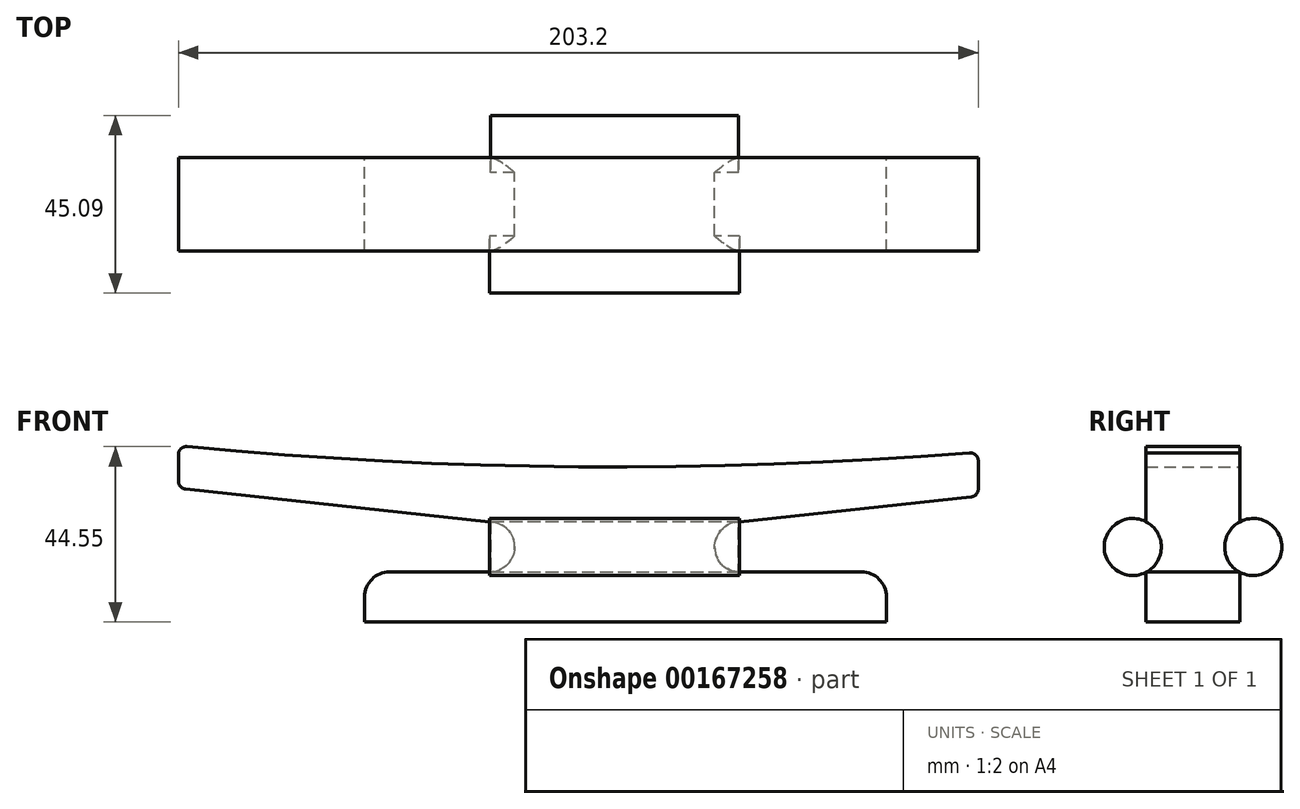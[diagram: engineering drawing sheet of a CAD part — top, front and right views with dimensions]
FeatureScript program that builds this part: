
annotation { "Feature Type Name" : "Feature", "Feature Type Description" : "" }
export const myFeature = defineFeature(function(context is Context, id is Id, definition is map)
    precondition{}
    {
        {
            var Q0;
            Q0=qCreatedBy(makeId("Front.planeOp"),FACE);
            var sketch = newSketch(context, id + "F0", { "sketchPlane" : qUnion([Q0])});
            skLineSegment(sketch, "E0", {"start": v(0, 28.03) * mm, "end": v(0, 38.16) * mm, "construction": true});
            skLineSegment(sketch, "E1", {"start": v(-63.5, -11.34) * mm, "end": v(-63.5, -4.99) * mm});
            skLineSegment(sketch, "E2", {"start": v(-57.15, 1.36) * mm, "end": v(-31.75, 1.36) * mm});
            skLineSegment(sketch, "E3", {"start": v(-31.07, 14.02) * mm, "end": v(-109, 22.4) * mm});
            skLineSegment(sketch, "E4", {"start": v(-110.81, 24.41) * mm, "end": v(-110.81, 31.18) * mm});
            skArc(sketch, "E5", {"start": v(-31.75, 1.36) * mm, "mid": v(-25.4, 7.37) * mm, "end": v(-31.07, 14.02) * mm});
            skArc(sketch, "E6.filletArc", {"start": v(-110.81, 24.41) * mm, "mid": v(-110.3, 23.06) * mm, "end": v(-109, 22.4) * mm});
            skPoint(sketch, "E7.visualSharp", {"position": v(-63.5, 1.36) * mm});
            skArc(sketch, "E7.filletArc", {"start": v(-57.15, 1.36) * mm, "mid": v(-61.64, -0.5) * mm, "end": v(-63.5, -4.99) * mm});
            skArc(sketch, "E8", {"start": v(-108.59, 33.2) * mm, "mid": v(-9.23, 28.07) * mm, "end": v(90.2, 31.6) * mm});
            skLineSegment(sketch, "E9", {"start": v(-63.5, -11.34) * mm, "end": v(0, -11.34) * mm});
            skPoint(sketch, "E10.newPointA", {"position": v(-101.6, 32.55) * mm});
            skArc(sketch, "E10.filletArc", {"start": v(-108.59, 33.2) * mm, "mid": v(-110.15, 32.68) * mm, "end": v(-110.81, 31.18) * mm});
            skLineSegment(sketch, "E11", {"start": v(0, -11.34) * mm, "end": v(69.04, -11.34) * mm});
            skLineSegment(sketch, "E12", {"start": v(69.04, -11.34) * mm, "end": v(69.04, -4.99) * mm});
            skLineSegment(sketch, "E13", {"start": v(62.69, 1.36) * mm, "end": v(31.75, 1.36) * mm});
            skPoint(sketch, "E14.visualSharp", {"position": v(69.04, 1.36) * mm});
            skArc(sketch, "E14.filletArc", {"start": v(69.04, -4.99) * mm, "mid": v(67.18, -0.5) * mm, "end": v(62.69, 1.36) * mm});
            skArc(sketch, "E15", {"start": v(31.07, 14.02) * mm, "mid": v(25.4, 7.37) * mm, "end": v(31.75, 1.36) * mm});
            skLineSegment(sketch, "E16", {"start": v(31.07, 14.02) * mm, "end": v(90.57, 20.41) * mm});
            skLineSegment(sketch, "E17", {"start": v(92.39, 22.43) * mm, "end": v(92.39, 29.57) * mm});
            skArc(sketch, "E18.filletArc", {"start": v(92.39, 29.57) * mm, "mid": v(91.73, 31.06) * mm, "end": v(90.2, 31.6) * mm});
            skPoint(sketch, "E19.visualSharp", {"position": v(92.39, 20.6) * mm});
            skArc(sketch, "E19.filletArc", {"start": v(90.57, 20.41) * mm, "mid": v(91.86, 21.08) * mm, "end": v(92.39, 22.43) * mm});
            skPoint(sketch, "E20.orphan", {"position": v(0, 0) * mm});
            skSolve(sketch);
        }
        {
            var Q0;
            Q0=makeQuery(id+"F0.imprint","IMPRINT",FACE,{"disambiguationData":[TD([[makeQuery(id+"F0.imprint","IMPRINT",EDGE,{"derivedFrom":sQuery(id+"F0.wireOp",EDGE,"E1")}),-1.0]])]});
            extrude(context, id + "F1", {"entities" : qUnion([Q0]), "depth" : 23.8 * mm});
        }
        {
            var Q0;
            Q0=qCreatedBy(makeId("Right.planeOp"),FACE);
            var sketch = newSketch(context, id + "F2", { "sketchPlane" : qUnion([Q0])});
            skCircle(sketch, "E21", {"center": v(3.4, 7.7) * mm, "radius": 7.25 * mm});
            skLineSegment(sketch, "E22", {"start": v(-11.9, 41.54) * mm, "end": v(-11.9, -15.53) * mm});
            skCircle(sketch, "E23", {"center": v(-27.2, 7.7) * mm, "radius": 7.25 * mm});
            skSolve(sketch);
        }
        {
            var Q0;
            Q0=makeQuery(id+"F2.imprint","IMPRINT",FACE,{"disambiguationData":[TD([[makeQuery(id+"F2.imprint","IMPRINT",EDGE,{"derivedFrom":sQuery(id+"F2.wireOp",EDGE,"E21")}),1.0]])]});
            extrude(context, id + "F3", {"entities" : qUnion([Q0]), "operationType" : NewBodyOperationType.ADD, "endBound" : BoundingType.SYMMETRIC, "depth" : 63 * mm});
        }
        {
            var Q0;
            Q0=makeQuery(id+"F2.imprint","IMPRINT",FACE,{"disambiguationData":[TD([[makeQuery(id+"F2.imprint","IMPRINT",EDGE,{"derivedFrom":sQuery(id+"F2.wireOp",EDGE,"E23")}),1.0]])]});
            var Q1;
            Q1=sQuery(id+"F2.wireOp",EDGE,"E23");
            extrude(context, id + "F4", {"entities" : qUnion([Q0]), "operationType" : NewBodyOperationType.ADD, "surfaceEntities" : qUnion([Q1]), "endBound" : BoundingType.SYMMETRIC, "depth" : 63.5 * mm});
        }
    });
